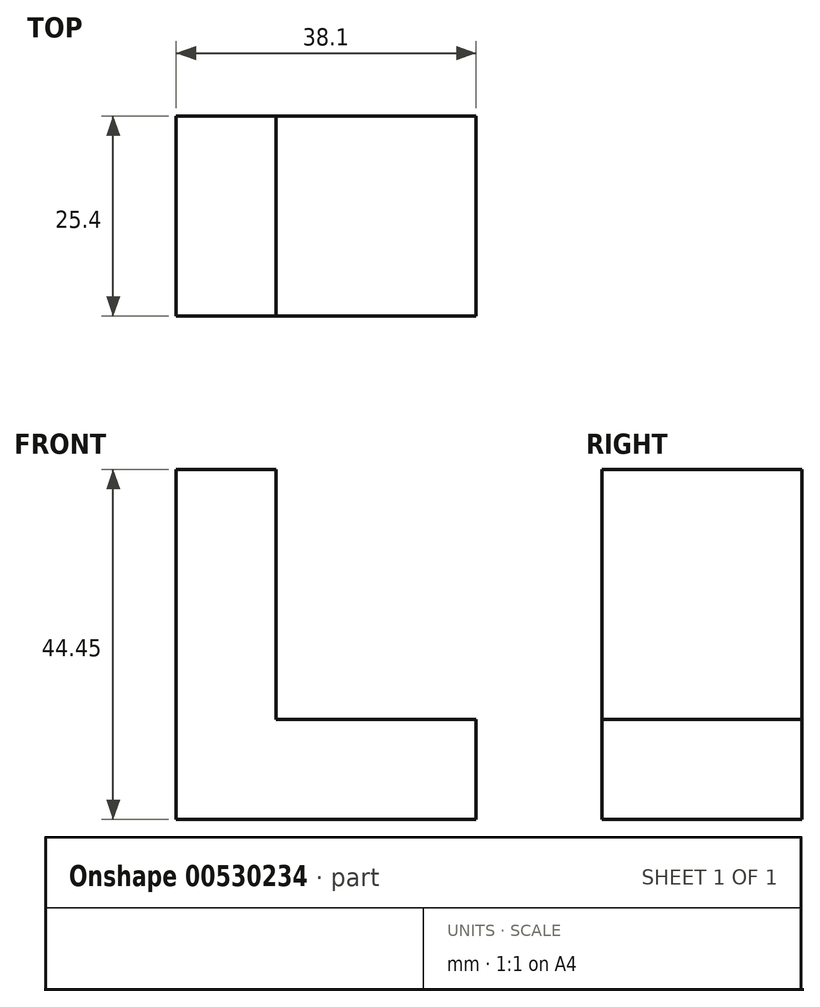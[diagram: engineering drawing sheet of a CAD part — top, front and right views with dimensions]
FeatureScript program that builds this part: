
annotation { "Feature Type Name" : "Feature", "Feature Type Description" : "" }
export const myFeature = defineFeature(function(context is Context, id is Id, definition is map)
    precondition{}
    {
        {
            var Q0;
            Q0=qCreatedBy(makeId("Front.planeOp"),FACE);
            var sketch = newSketch(context, id + "F0", { "sketchPlane" : qUnion([Q0])});
            skLineSegment(sketch, "E0", {"start": v(-119.54, 0) * mm, "end": v(-119.54, 44.45) * mm});
            skLineSegment(sketch, "E1", {"start": v(-119.54, 0) * mm, "end": v(-81.44, 0) * mm});
            skLineSegment(sketch, "E2", {"start": v(-81.44, 0) * mm, "end": v(-81.44, 12.7) * mm});
            skLineSegment(sketch, "E3", {"start": v(-81.44, 12.7) * mm, "end": v(-106.84, 12.7) * mm});
            skLineSegment(sketch, "E4", {"start": v(-106.84, 12.7) * mm, "end": v(-106.84, 44.45) * mm});
            skLineSegment(sketch, "E5", {"start": v(-106.84, 44.45) * mm, "end": v(-119.54, 44.45) * mm});
            skSolve(sketch);
        }
        {
            var Q0;
            Q0 = qSketchRegion(id + "F0", true);
            extrude(context, id + "F1", {"entities" : qUnion([Q0]), "depth" : 25.4 * mm, "offsetDistance" : 25.4 * mm});
        }
    });
